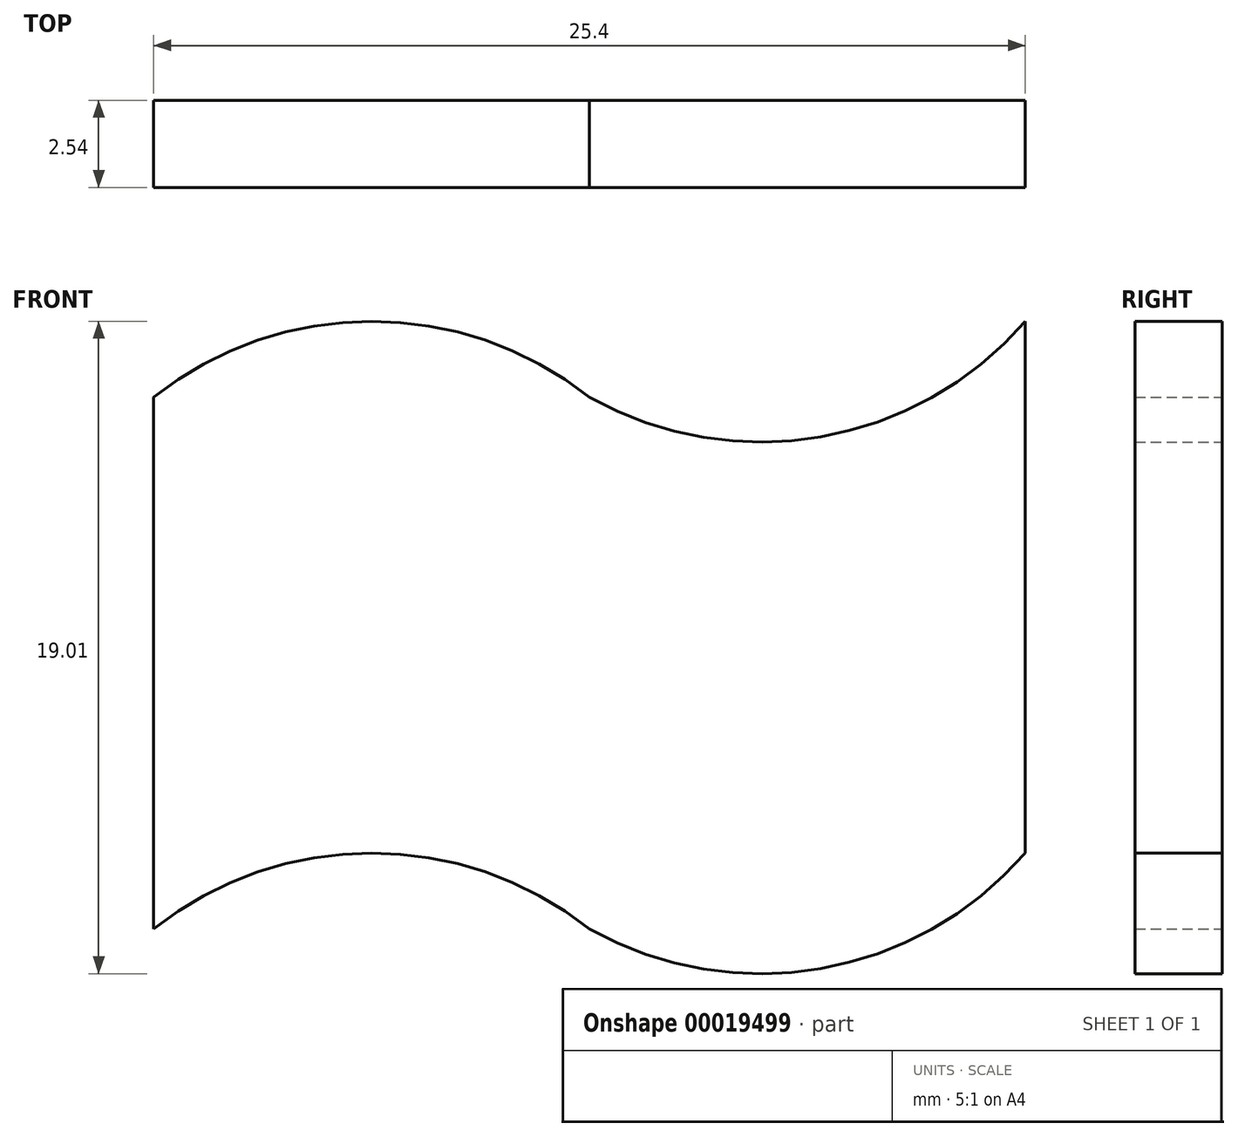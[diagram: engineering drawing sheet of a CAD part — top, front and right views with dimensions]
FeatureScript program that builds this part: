
annotation { "Feature Type Name" : "Feature", "Feature Type Description" : "" }
export const myFeature = defineFeature(function(context is Context, id is Id, definition is map)
    precondition{}
    {
        {
            var Q0;
            Q0=qCreatedBy(makeId("Front.planeOp"),FACE);
            var sketch = newSketch(context, id + "F0", { "sketchPlane" : qUnion([Q0])});
            skLineSegment(sketch, "E0", {"start": v(-9.6, 15.5) * mm, "end": v(-9.6, 0) * mm});
            skArc(sketch, "E1", {"start": v(3.1, 15.5) * mm, "mid": v(-3.26, 17.7) * mm, "end": v(-9.6, 15.5) * mm});
            skArc(sketch, "E2", {"start": v(3.1, 0) * mm, "mid": v(-3.26, 2.21) * mm, "end": v(-9.6, 0) * mm});
            skLineSegment(sketch, "E3", {"start": v(-3.26, 17.7) * mm, "end": v(-9.6, 17.7) * mm, "construction": true});
            skLineSegment(sketch, "E4", {"start": v(-9.6, 17.7) * mm, "end": v(-9.6, 15.5) * mm, "construction": true});
            skLineSegment(sketch, "E5", {"start": v(-9.6, 17.7) * mm, "end": v(15.8, 17.7) * mm, "construction": true});
            skArc(sketch, "E6", {"start": v(3.1, 15.5) * mm, "mid": v(9.83, 14.34) * mm, "end": v(15.8, 17.7) * mm});
            skLineSegment(sketch, "E7", {"start": v(15.8, 17.7) * mm, "end": v(15.8, 2.21) * mm});
            skArc(sketch, "E8", {"start": v(3.1, 0) * mm, "mid": v(9.83, -1.15) * mm, "end": v(15.8, 2.21) * mm});
            skSolve(sketch);
        }
        {
            var Q0;
            Q0=makeQuery(id+"F0.imprint","IMPRINT",FACE,{"disambiguationData":[TD([[makeQuery(id+"F0.imprint","IMPRINT",EDGE,{"derivedFrom":sQuery(id+"F0.wireOp",EDGE,"E0")}),1.0]])]});
            extrude(context, id + "F1", {"entities" : qUnion([Q0]), "depth" : 2.54 * mm});
        }
    });
